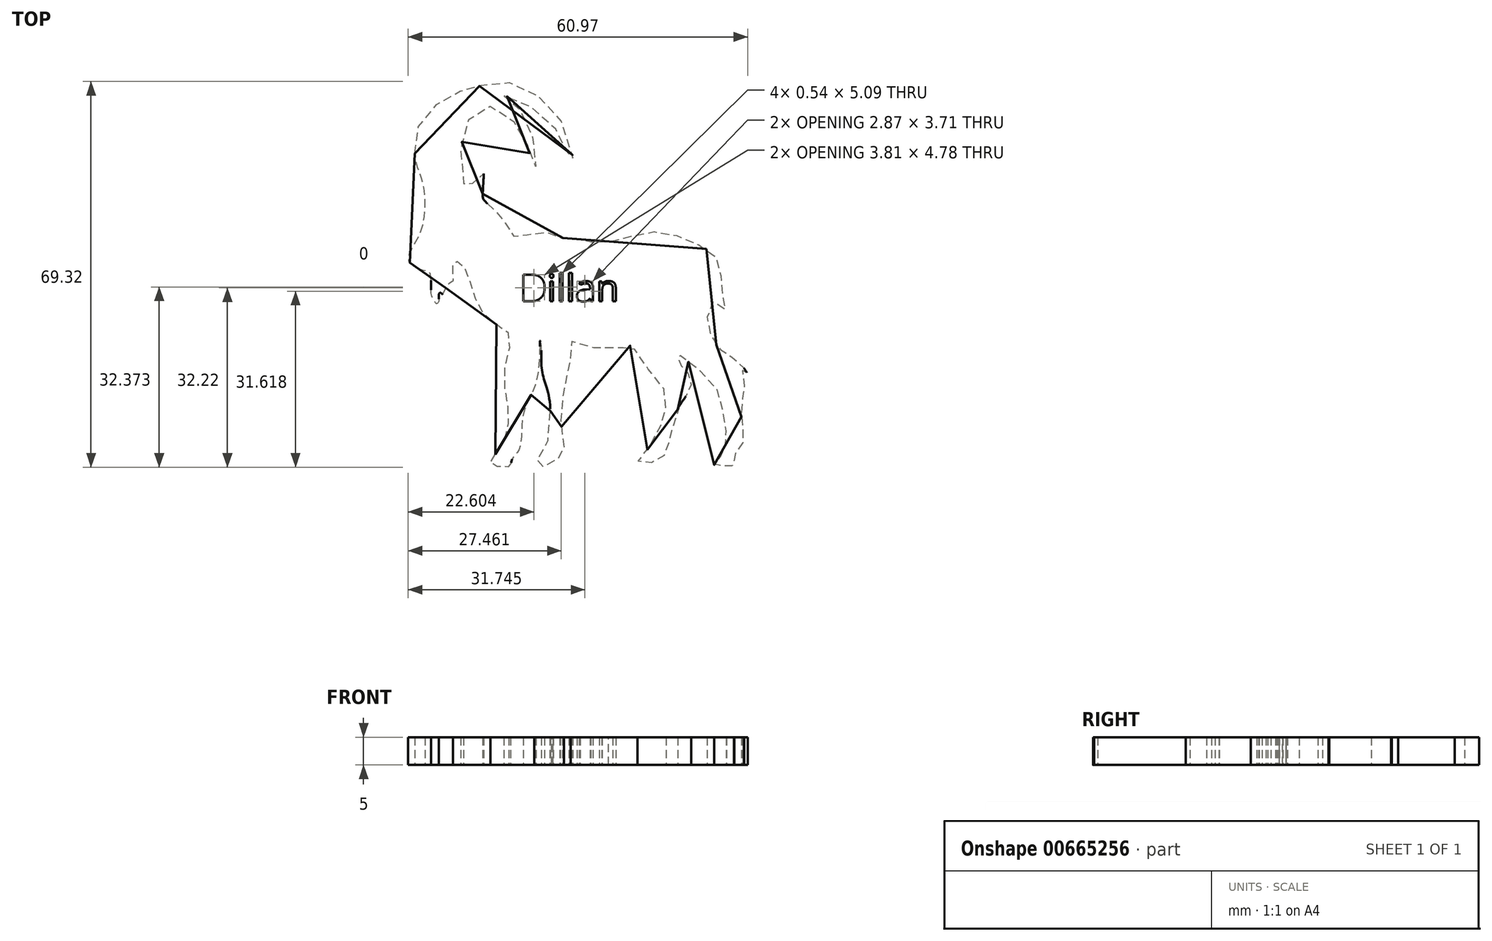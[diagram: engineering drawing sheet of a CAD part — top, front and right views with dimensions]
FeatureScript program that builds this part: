
annotation { "Feature Type Name" : "Feature", "Feature Type Description" : "" }
export const myFeature = defineFeature(function(context is Context, id is Id, definition is map)
    precondition{}
    {
        {
            var Q0;
            Q0=qCreatedBy(makeId("Top.planeOp"),FACE);
            var sketch = newSketch(context, id + "F0", { "sketchPlane" : qUnion([Q0])});
            skPoint(sketch, "E0.162.internal.snap0", {"position": v(-61.53, 35.5) * mm});
            skFitSpline(sketch, "E0", {"points": [v(-59.75, 56.9) * mm, v(-59.66, 59.67) * mm, v(-58.7, 62.54) * mm, v(-56.45, 65.2) * mm, v(-54.26, 66.85) * mm, v(-51.55, 68.12) * mm, v(-49.18, 68.53) * mm, v(-48.37, 68.94) * mm, v(-45.9, 69.75) * mm, v(-42.22, 69.53) * mm, v(-38.8, 68.1) * mm, v(-34.7, 64.47) * mm, v(-32.8, 61.2) * mm, v(-31.43, 55.68) * mm, v(-31.84, 55.37) * mm, v(-32.24, 56.43) * mm, v(-33.05, 58.27) * mm, v(-33.77, 59.89) * mm, v(-35.14, 62.3) * mm, v(-38.95, 65.29) * mm, v(-42.6, 67) * mm, v(-43.78, 67.22) * mm, v(-42.85, 66.69) * mm, v(-40.79, 64.63) * mm, v(-38.95, 61.1) * mm, v(-38.3, 57.96) * mm, v(-38.04, 54.56) * mm, v(-38.32, 54.21) * mm, v(-39.26, 57.55) * mm, v(-40.38, 60.36) * mm, v(-42.13, 62.82) * mm, v(-44.56, 64.72) * mm, v(-48.06, 65.38) * mm, v(-49.99, 63.2) * mm, v(-51.2, 59.58) * mm, v(-51.49, 55.68) * mm, v(-50.99, 51.37) * mm, v(-50.93, 50.94) * mm, v(-50.02, 50.47) * mm, v(-49.37, 51.53) * mm, v(-47.56, 54.06) * mm, v(-47.43, 53.34) * mm, v(-47.4, 53.18) * mm, v(-47.56, 49.4) * mm, v(-47.28, 48.47) * mm, v(-46.06, 47.26) * mm, v(-45.15, 46.45) * mm, v(-42.79, 43.32) * mm, v(-41.46, 41.74) * mm, v(-37.46, 42.9) * mm, v(-33.6, 41.79) * mm, v(-32.3, 41.74) * mm, v(-28.3, 41.08) * mm, v(-23.64, 41.24) * mm, v(-16.8, 42.82) * mm, v(-10.06, 41.08) * mm, v(-5.23, 37.58) * mm, v(-4.65, 31.92) * mm, v(-3.9, 28.84) * mm, v(-6.07, 30.25) * mm, v(-7.23, 27.09) * mm, v(-6.07, 23.17) * mm, v(-3.49, 20.6) * mm, v(-1.65, 19.6) * mm, v(0, 17.18) * mm, v(-0.83, 17.92) * mm, v(-0.62, 15.68) * mm, v(-0.8, 13.68) * mm, v(-0.97, 11.86) * mm, v(-1.1, 9.05) * mm, v(-0.7, 6.8) * mm, v(-0.97, 4.62) * mm, v(-2.18, 3) * mm, v(-2.4, 2.31) * mm, v(-2.38, 1.77) * mm, v(-2.47, 1.34) * mm, v(-2.46, 0.85) * mm, v(-2.78, 0.72) * mm, v(-2.95, 0.71) * mm, v(-4.69, 0.75) * mm, v(-5.9, 0.8) * mm, v(-5.93, 1.1) * mm, v(-5.4, 1.7) * mm, v(-4.55, 2.87) * mm, v(-3.86, 5.08) * mm, v(-3.81, 6.75) * mm, v(-4.55, 11.3) * mm, v(-6.55, 16.04) * mm, v(-12.16, 20.66) * mm, v(-12.43, 20.9) * mm, v(-12.48, 20.62) * mm, v(-12.48, 19.7) * mm, v(-12.13, 18.97) * mm, v(-11.36, 18.23) * mm, v(-10.64, 17.33) * mm, v(-10.1, 15.9) * mm, v(-10.43, 14.35) * mm, v(-11.54, 12.6) * mm, v(-12.53, 10.82) * mm, v(-13.76, 6.53) * mm, v(-14.12, 5.27) * mm, v(-14.63, 2.73) * mm, v(-14.88, 2.64) * mm, v(-16.87, 1.35) * mm, v(-17.13, 1.35) * mm, v(-19.74, 1.38) * mm, v(-19.7, 1.52) * mm, v(-18.7, 2.76) * mm, v(-16.28, 6.45) * mm, v(-14.88, 10.1) * mm, v(-14.61, 12.36) * mm, v(-15.7, 15.88) * mm, v(-19.46, 20) * mm, v(-20.7, 22.35) * mm, v(-22, 22.06) * mm, v(-28.82, 22.24) * mm, v(-31.7, 23.06) * mm, v(-31.77, 20.82) * mm, v(-33.42, 12.17) * mm, v(-33.3, 6.7) * mm, v(-33.18, 2.4) * mm, v(-33.95, 2.1) * mm, v(-35.42, 0.8) * mm, v(-38.24, 0.98) * mm, v(-37.71, 1.8) * mm, v(-35.83, 5.4) * mm, v(-35.65, 13.1) * mm, v(-36.54, 16.28) * mm, v(-37.03, 19.23) * mm, v(-37.03, 22.18) * mm, v(-37.17, 22.92) * mm, v(-37.27, 23.21) * mm, v(-37.8, 16.56) * mm, v(-40.26, 10.03) * mm, v(-40.97, 3.86) * mm, v(-42.2, 2.1) * mm, v(-42.5, 1.07) * mm, v(-42.74, 0.67) * mm, v(-44.78, 0.6) * mm, v(-46.18, 1.28) * mm, v(-45.73, 2.19) * mm, v(-44.24, 4.76) * mm, v(-43.44, 6.26) * mm, v(-42.88, 10.25) * mm, v(-43.68, 17.83) * mm, v(-42.69, 24.16) * mm, v(-46.36, 27) * mm, v(-49.23, 31.85) * mm, v(-50.91, 36.5) * mm, v(-52.3, 37.5) * mm, v(-52.93, 37.18) * mm, v(-53, 33.53) * mm, v(-53.48, 33.49) * mm, v(-53.9, 33.53) * mm, v(-54.42, 32.07) * mm, v(-54.77, 31.56) * mm, v(-55, 31.8) * mm, v(-55.36, 31.76) * mm, v(-55.48, 30.34) * mm, v(-55.83, 29.91) * mm, v(-56.15, 30.19) * mm, v(-56.82, 31.72) * mm, v(-57.05, 35.5) * mm, v(-58.24, 35.88) * mm, v(-60.28, 36.88) * mm, v(-60.94, 38.13) * mm, v(-59.4, 41.33) * mm, v(-58.03, 45.58) * mm, v(-58.15, 50.9) * mm, v(-58.83, 53.26) * mm, v(-59.59, 55.48) * mm, v(-59.75, 56.9) * mm]});
            skText(sketch, "E1", { "text": "Dillan", "fontName": "OpenSans-Regular.ttf"});
            const initialGuessF0  = {"E1": [-0.04091, 0.03034, 1, 0, 0.00482]};
            skSetInitialGuess(sketch, initialGuessF0);
            skSolve(sketch);
        }
        {
            var Q0;
            Q0 = qSketchRegion(id + "F0", true);
            extrude(context, id + "F1", {"entities" : qUnion([Q0]), "depth" : 5 * mm, "offsetDistance" : 25.4 * mm});
        }
    });
